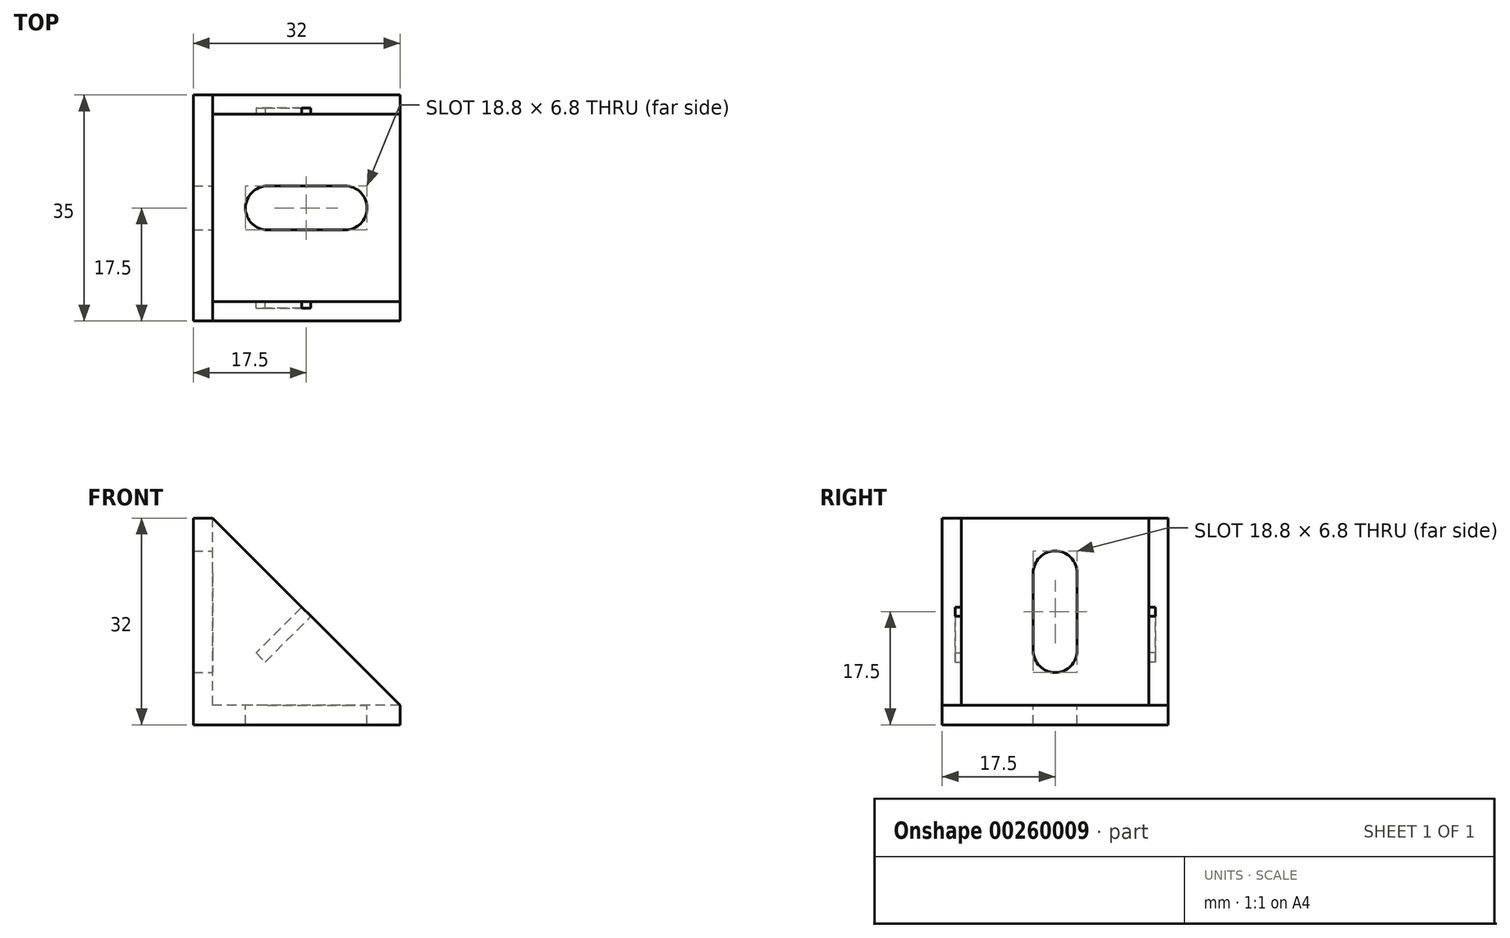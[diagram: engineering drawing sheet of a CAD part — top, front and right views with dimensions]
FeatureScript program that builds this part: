
annotation { "Feature Type Name" : "Feature", "Feature Type Description" : "" }
export const myFeature = defineFeature(function(context is Context, id is Id, definition is map)
    precondition{}
    {
        {
            var Q0;
            Q0=qCreatedBy(makeId("Front.planeOp"),FACE);
            var sketch = newSketch(context, id + "F0", { "sketchPlane" : qUnion([Q0])});
            skLineSegment(sketch, "E0", {"start": v(0, 0) * mm, "end": v(0, 32) * mm});
            skLineSegment(sketch, "E1", {"start": v(3, 32) * mm, "end": v(32, 3) * mm});
            skLineSegment(sketch, "E2", {"start": v(32, 0) * mm, "end": v(0, 0) * mm});
            skLineSegment(sketch, "E3", {"start": v(0, 32) * mm, "end": v(3, 32) * mm});
            skLineSegment(sketch, "E4", {"start": v(32, 0) * mm, "end": v(32, 3) * mm});
            skSolve(sketch);
        }
        {
            var Q0;
            Q0=makeQuery(id+"F0.imprint","IMPRINT",FACE,{"disambiguationData":[TD([[makeQuery(id+"F0.imprint","IMPRINT",EDGE,{"derivedFrom":sQuery(id+"F0.wireOp",EDGE,"E0")}),-1.0]])]});
            extrude(context, id + "F1", {"entities" : qUnion([Q0]), "depth" : 35 * mm});
        }
        {
            var Q0;
            Q0=makeQuery(id+"F1.opExtrude","SWEPT_FACE",FACE,{"disambiguationData":[OSD([sQuery(id+"F0.wireOp",EDGE,"E3")])]});
            var Q1;
            Q1=makeQuery(id+"F1.opExtrude","SWEPT_FACE",FACE,{"disambiguationData":[OSD([sQuery(id+"F0.wireOp",EDGE,"E1")])]});
            var Q2;
            Q2=makeQuery(id+"F1.opExtrude","SWEPT_FACE",FACE,{"disambiguationData":[OSD([sQuery(id+"F0.wireOp",EDGE,"E4")])]});
            shell(context, id + "F2", {"entities" : qUnion([Q0, Q1, Q2]), "thickness" : 3 * mm});
        }
        {
            var Q0;
            Q0=makeQuery(id+"F2.opShell","OFFSET_FACE",FACE,{"disambiguationData":[OSD([sQuery(id+"F0.wireOp",EDGE,"E2")])]});
            var sketch = newSketch(context, id + "F3", { "sketchPlane" : qUnion([Q0])});
            skArc(sketch, "E5", {"start": v(23.5, -20.9) * mm, "mid": v(26.9, -17.5) * mm, "end": v(23.5, -14.1) * mm});
            skPoint(sketch, "E5.centerSnap0", {"position": v(32, -17.5) * mm});
            skArc(sketch, "E6", {"start": v(11.5, -14.1) * mm, "mid": v(8.1, -17.5) * mm, "end": v(11.5, -20.9) * mm});
            skLineSegment(sketch, "E7", {"start": v(11.5, -14.1) * mm, "end": v(23.5, -14.1) * mm});
            skLineSegment(sketch, "E8", {"start": v(23.5, -20.9) * mm, "end": v(11.5, -20.9) * mm});
            skPoint(sketch, "E9.startSnap0", {"position": v(17.5, -3) * mm});
            skPoint(sketch, "E9.endSnap0", {"position": v(17.5, -32) * mm});
            skSolve(sketch);
        }
        {
            var Q0;
            Q0=makeQuery(id+"F3.imprint","IMPRINT",FACE,{"disambiguationData":[TD([[makeQuery(id+"F3.imprint","IMPRINT",EDGE,{"derivedFrom":sQuery(id+"F3.wireOp",EDGE,"E5")}),1.0]])]});
            extrude(context, id + "F4", {"entities" : qUnion([Q0]), "operationType" : NewBodyOperationType.REMOVE, "oppositeDirection" : true, "depth" : 3 * mm});
        }
        {
            var Q0;
            Q0=makeQuery(id+"F2.opShell","OFFSET_FACE",FACE,{"disambiguationData":[OSD([sQuery(id+"F0.wireOp",EDGE,"E0")])]});
            var sketch = newSketch(context, id + "F5", { "sketchPlane" : qUnion([Q0])});
            skLineSegment(sketch, "E10", {"start": v(1.93, 17.5) * mm, "end": v(-37.41, 17.5) * mm, "construction": true});
            skPoint(sketch, "E10.startSnap0", {"position": v(-3, 17.5) * mm});
            skPoint(sketch, "E10.endSnap0", {"position": v(-32, 17.5) * mm});
            skArc(sketch, "E11", {"start": v(-14.1, 23.5) * mm, "mid": v(-17.5, 26.9) * mm, "end": v(-20.9, 23.5) * mm});
            skPoint(sketch, "E11.centerSnap0", {"position": v(-17.5, 32) * mm});
            skArc(sketch, "E12", {"start": v(-20.9, 11.5) * mm, "mid": v(-17.5, 8.1) * mm, "end": v(-14.1, 11.5) * mm});
            skLineSegment(sketch, "E13", {"start": v(-14.1, 23.5) * mm, "end": v(-14.1, 11.5) * mm});
            skLineSegment(sketch, "E14", {"start": v(-20.9, 11.5) * mm, "end": v(-20.9, 23.5) * mm});
            skSolve(sketch);
        }
        {
            var Q0;
            Q0=makeQuery(id+"F5.imprint","IMPRINT",FACE,{"disambiguationData":[TD([[makeQuery(id+"F5.imprint","IMPRINT",EDGE,{"derivedFrom":sQuery(id+"F5.wireOp",EDGE,"E11")}),1.0]])]});
            extrude(context, id + "F6", {"entities" : qUnion([Q0]), "operationType" : NewBodyOperationType.REMOVE, "oppositeDirection" : true, "depth" : 3 * mm});
        }
        {
            var Q0;
            {var subQ0=sQuery(id+"F0.wireOp",EDGE,"E4");var subQ1=sQuery(id+"F0.wireOp",EDGE,"E3");var subQ2=sQuery(id+"F0.wireOp",EDGE,"E2");var subQ3=sQuery(id+"F0.wireOp",EDGE,"E1");var subQ4=sQuery(id+"F0.wireOp",EDGE,"E0");Q0=makeQuery(id+"F2.opShell","OFFSET_FACE",FACE,{"disambiguationData":[OSD([subQ4,subQ3,subQ2,subQ1,subQ0]),TDD([makeQuery(id+"F1.opExtrude","CAP_FACE",FACE,{"disambiguationData":[OSD([subQ4,subQ3,subQ2,subQ1,subQ0])],"isStart":true})])]});}
            var sketch = newSketch(context, id + "F7", { "sketchPlane" : qUnion([Q0])});
            skLineSegment(sketch, "E15", {"start": v(3, 3) * mm, "end": v(111.5, 111.5) * mm, "construction": true});
            skLineSegment(sketch, "E16", {"start": v(18.2, 16.8) * mm, "end": v(16.8, 18.2) * mm});
            skLineSegment(sketch, "E17", {"start": v(16.8, 18.2) * mm, "end": v(9.72, 11.14) * mm});
            skPoint(sketch, "E18", {"position": v(17.5, 17.5) * mm});
            skLineSegment(sketch, "E19", {"start": v(9.72, 11.14) * mm, "end": v(11.14, 9.72) * mm});
            skLineSegment(sketch, "E20", {"start": v(11.14, 9.72) * mm, "end": v(18.2, 16.8) * mm});
            skSolve(sketch);
        }
        {
            var Q0;
            Q0=makeQuery(id+"F7.imprint","IMPRINT",FACE,{"disambiguationData":[TD([[makeQuery(id+"F7.imprint","IMPRINT",EDGE,{"derivedFrom":sQuery(id+"F7.wireOp",EDGE,"E16")}),-1.0]])]});
            extrude(context, id + "F8", {"entities" : qUnion([Q0]), "operationType" : NewBodyOperationType.REMOVE, "oppositeDirection" : true, "offsetDistance" : 25 * mm, "depth" : 1 * mm});
        }
        {
            var Q0;
            {var subQ0=sQuery(id+"F0.wireOp",EDGE,"E4");var subQ1=sQuery(id+"F0.wireOp",EDGE,"E3");var subQ2=sQuery(id+"F0.wireOp",EDGE,"E2");var subQ3=sQuery(id+"F0.wireOp",EDGE,"E1");var subQ4=sQuery(id+"F0.wireOp",EDGE,"E0");Q0=makeQuery(id+"F2.opShell","OFFSET_FACE",FACE,{"disambiguationData":[OSD([subQ4,subQ3,subQ2,subQ1,subQ0]),TDD([makeQuery(id+"F1.opExtrude","CAP_FACE",FACE,{"disambiguationData":[OSD([subQ4,subQ3,subQ2,subQ1,subQ0])],"isStart":false})])]});}
            var sketch = newSketch(context, id + "F9", { "sketchPlane" : qUnion([Q0])});
            skLineSegment(sketch, "E21", {"start": v(-3, 3) * mm, "end": v(-17.5, 17.5) * mm, "construction": true});
            skLineSegment(sketch, "E22", {"start": v(-18.2, 16.8) * mm, "end": v(-16.8, 18.2) * mm});
            skLineSegment(sketch, "E23", {"start": v(-16.8, 18.2) * mm, "end": v(-9.72, 11.14) * mm});
            skLineSegment(sketch, "E24", {"start": v(-9.72, 11.14) * mm, "end": v(-11.14, 9.72) * mm});
            skLineSegment(sketch, "E25", {"start": v(-11.14, 9.72) * mm, "end": v(-18.2, 16.8) * mm});
            skPoint(sketch, "E26", {"position": v(-17.5, 17.5) * mm});
            skSolve(sketch);
        }
        {
            var Q0;
            Q0=makeQuery(id+"F9.imprint","IMPRINT",FACE,{"disambiguationData":[TD([[makeQuery(id+"F9.imprint","IMPRINT",EDGE,{"derivedFrom":sQuery(id+"F9.wireOp",EDGE,"E22")}),1.0]])]});
            extrude(context, id + "F10", {"entities" : qUnion([Q0]), "operationType" : NewBodyOperationType.REMOVE, "oppositeDirection" : true, "depth" : 1 * mm});
        }
    });
